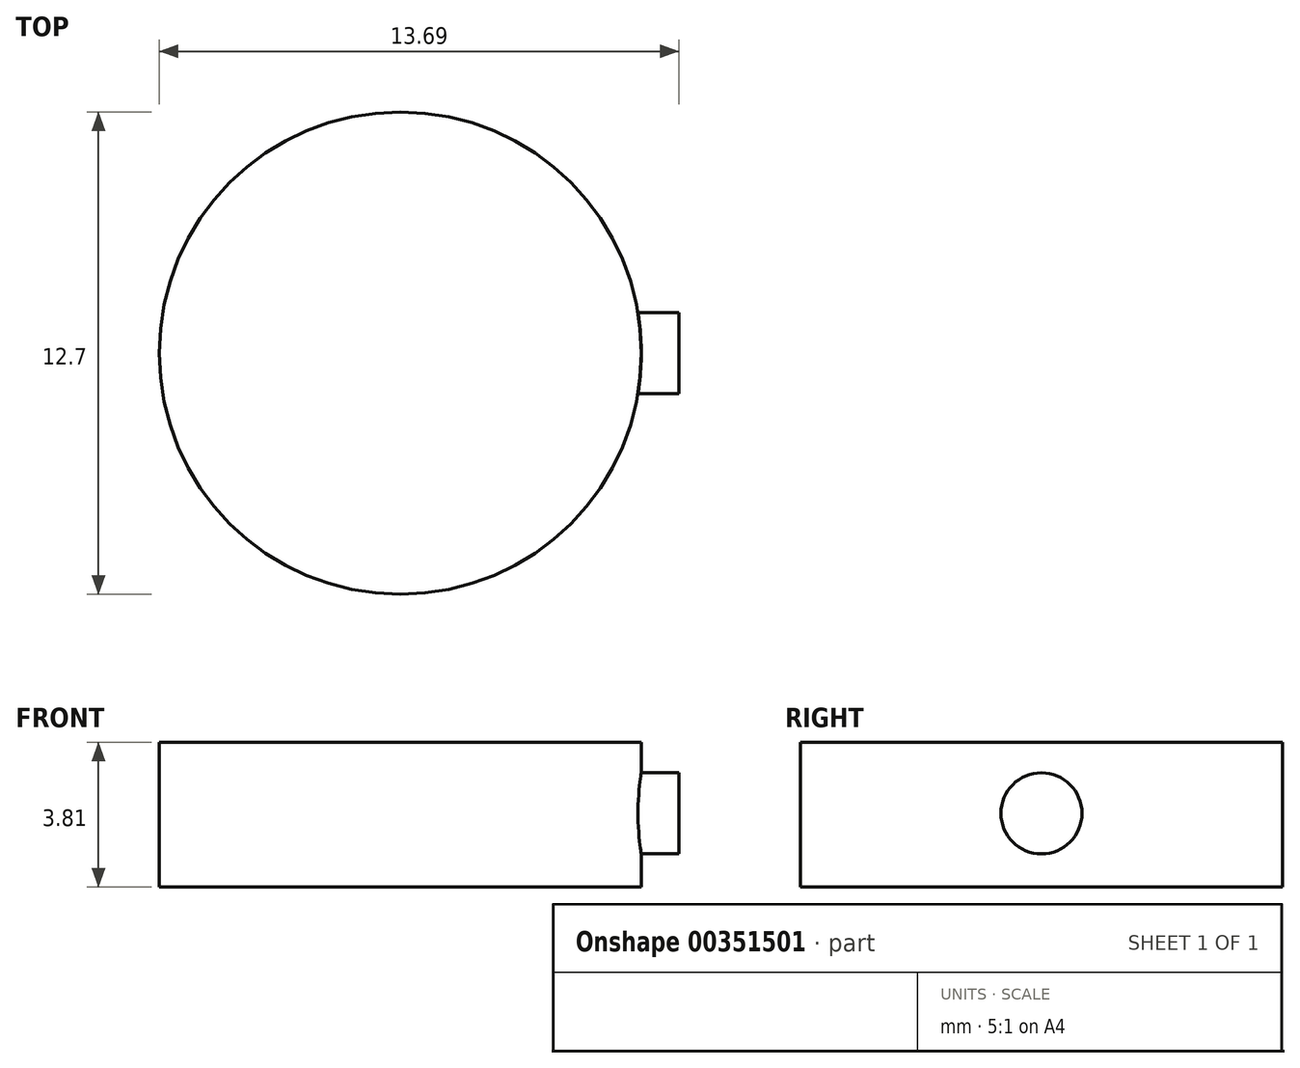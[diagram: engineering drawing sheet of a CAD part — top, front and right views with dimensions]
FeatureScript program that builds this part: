
annotation { "Feature Type Name" : "Feature", "Feature Type Description" : "" }
export const myFeature = defineFeature(function(context is Context, id is Id, definition is map)
    precondition{}
    {
        {
            var Q0;
            Q0=qCreatedBy(makeId("Front.planeOp"),FACE);
            var sketch = newSketch(context, id + "F0", { "sketchPlane" : qUnion([Q0])});
            skLineSegment(sketch, "E0.bottom", {"start": v(0, 0) * mm, "end": v(6.35, 0) * mm});
            skLineSegment(sketch, "E0.top", {"start": v(0, 3.81) * mm, "end": v(6.35, 3.81) * mm});
            skLineSegment(sketch, "E0.left", {"start": v(0, 0) * mm, "end": v(0, 3.81) * mm});
            skLineSegment(sketch, "E0.right", {"start": v(6.35, 0) * mm, "end": v(6.35, 3.81) * mm});
            skSolve(sketch);
        }
        {
            var Q0;
            Q0=makeQuery(id+"F0.imprint","IMPRINT",FACE,{"disambiguationData":[TD([[makeQuery(id+"F0.imprint","IMPRINT",EDGE,{"derivedFrom":sQuery(id+"F0.wireOp",EDGE,"E0.bottom")}),1.0]])]});
            var Q1;
            Q1=sQuery(id+"F0.wireOp",EDGE,"E0.left");
            revolve(context, id + "F1", {"entities" : qUnion([Q0]), "axis" : qUnion([Q1]), "revolveType" : RevolveType.FULL});
        }
        {
            var Q0;
            Q0=qCreatedBy(makeId("Right.planeOp"),FACE);
            var sketch = newSketch(context, id + "F2", { "sketchPlane" : qUnion([Q0])});
            skCircle(sketch, "E1", {"center": v(0, 1.94) * mm, "radius": 1.07 * mm});
            skSolve(sketch);
        }
        {
            var Q0;
            Q0 = qSketchRegion(id + "F2", true);
            extrude(context, id + "F3", {"entities" : qUnion([Q0]), "operationType" : NewBodyOperationType.ADD, "depth" : 7.34 * mm});
        }
    });
